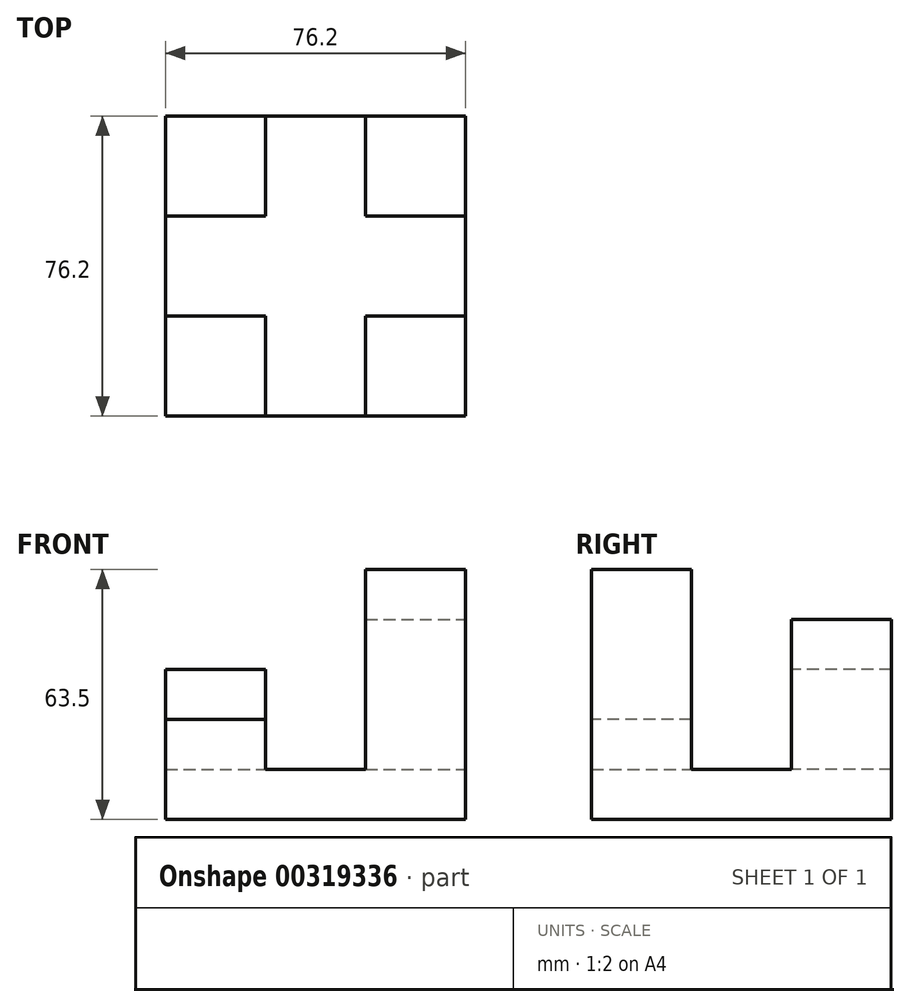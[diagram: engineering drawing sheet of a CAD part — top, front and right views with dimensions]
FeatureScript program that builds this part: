
annotation { "Feature Type Name" : "Feature", "Feature Type Description" : "" }
export const myFeature = defineFeature(function(context is Context, id is Id, definition is map)
    precondition{}
    {
        {
            var Q0;
            Q0=qCreatedBy(makeId("Top.planeOp"),FACE);
            var sketch = newSketch(context, id + "F0", { "sketchPlane" : qUnion([Q0])});
            skLineSegment(sketch, "E0.bottom", {"start": v(-38.59, 41.6) * mm, "end": v(37.61, 41.6) * mm});
            skLineSegment(sketch, "E0.top", {"start": v(-38.59, -34.6) * mm, "end": v(37.61, -34.6) * mm});
            skLineSegment(sketch, "E0.left", {"start": v(-38.59, 41.6) * mm, "end": v(-38.59, -34.6) * mm});
            skLineSegment(sketch, "E0.right", {"start": v(37.61, 41.6) * mm, "end": v(37.61, -34.6) * mm});
            skSolve(sketch);
        }
        {
            var Q0;
            Q0 = qSketchRegion(id + "F0", true);
            extrude(context, id + "F1", {"entities" : qUnion([Q0]), "depth" : 12.7 * mm});
        }
        {
            var Q0;
            Q0=makeQuery(id+"F1.opExtrude","CAP_FACE",FACE,{"disambiguationData":[OSD([sQuery(id+"F0.wireOp",EDGE,"E0.bottom"),sQuery(id+"F0.wireOp",EDGE,"E0.top"),sQuery(id+"F0.wireOp",EDGE,"E0.left"),sQuery(id+"F0.wireOp",EDGE,"E0.right")])],"isStart":false});
            var sketch = newSketch(context, id + "F2", { "sketchPlane" : qUnion([Q0])});
            skLineSegment(sketch, "E1", {"start": v(-38.59, -9.2) * mm, "end": v(-13.19, -9.2) * mm});
            skLineSegment(sketch, "E2", {"start": v(-13.19, -9.2) * mm, "end": v(-13.19, -34.6) * mm});
            skLineSegment(sketch, "E3", {"start": v(-13.19, -34.6) * mm, "end": v(-38.59, -34.6) * mm});
            skLineSegment(sketch, "E4", {"start": v(-38.59, -34.6) * mm, "end": v(-38.59, -9.2) * mm});
            skSolve(sketch);
        }
        {
            var Q0;
            Q0 = qSketchRegion(id + "F2", true);
            extrude(context, id + "F3", {"entities" : qUnion([Q0]), "operationType" : NewBodyOperationType.ADD, "depth" : 12.7 * mm});
        }
        {
            var Q0;
            Q0=makeQuery(id+"F1.opExtrude","CAP_FACE",FACE,{"disambiguationData":[OSD([sQuery(id+"F0.wireOp",EDGE,"E0.bottom"),sQuery(id+"F0.wireOp",EDGE,"E0.top"),sQuery(id+"F0.wireOp",EDGE,"E0.left"),sQuery(id+"F0.wireOp",EDGE,"E0.right")])],"isStart":false});
            var sketch = newSketch(context, id + "F4", { "sketchPlane" : qUnion([Q0])});
            skLineSegment(sketch, "E5", {"start": v(-38.59, 16.2) * mm, "end": v(-13.19, 16.2) * mm});
            skLineSegment(sketch, "E6", {"start": v(-13.19, 16.2) * mm, "end": v(-13.19, 41.6) * mm});
            skLineSegment(sketch, "E7", {"start": v(-13.19, 41.6) * mm, "end": v(-38.59, 41.6) * mm});
            skSolve(sketch);
        }
        {
            var Q0;
            Q0 = qSketchRegion(id + "F4", true);
            var Q1;
            {var subQ0=sQuery(id+"F4.wireOp",EDGE,"E5");Q1=makeQuery(id+"F4.imprint","IMPRINT",FACE,{"disambiguationData":[TD([[makeQuery(id+"F4.imprint","IMPRINT",EDGE,{"derivedFrom":subQ0}),1.0]])]});}
            extrude(context, id + "F5", {"entities" : qUnion([Q0, Q1]), "depth" : 25.4 * mm});
        }
        {
            var Q0;
            Q0=makeQuery(id+"F1.opExtrude","CAP_FACE",FACE,{"disambiguationData":[OSD([sQuery(id+"F0.wireOp",EDGE,"E0.bottom"),sQuery(id+"F0.wireOp",EDGE,"E0.top"),sQuery(id+"F0.wireOp",EDGE,"E0.left"),sQuery(id+"F0.wireOp",EDGE,"E0.right")])],"isStart":false});
            var sketch = newSketch(context, id + "F6", { "sketchPlane" : qUnion([Q0])});
            skLineSegment(sketch, "E8", {"start": v(12.21, 41.6) * mm, "end": v(12.21, 16.2) * mm});
            skLineSegment(sketch, "E9", {"start": v(12.21, 16.2) * mm, "end": v(37.61, 16.2) * mm});
            skLineSegment(sketch, "E10", {"start": v(37.61, 16.2) * mm, "end": v(37.61, 41.6) * mm});
            skLineSegment(sketch, "E11", {"start": v(37.61, 41.6) * mm, "end": v(12.21, 41.6) * mm});
            skSolve(sketch);
        }
        {
            var Q0;
            Q0 = qSketchRegion(id + "F6", true);
            extrude(context, id + "F7", {"entities" : qUnion([Q0]), "operationType" : NewBodyOperationType.ADD, "depth" : 38.1 * mm});
        }
        {
            var Q0;
            Q0=makeQuery(id+"F1.opExtrude","CAP_FACE",FACE,{"disambiguationData":[OSD([sQuery(id+"F0.wireOp",EDGE,"E0.bottom"),sQuery(id+"F0.wireOp",EDGE,"E0.top"),sQuery(id+"F0.wireOp",EDGE,"E0.left"),sQuery(id+"F0.wireOp",EDGE,"E0.right")])],"isStart":false});
            var sketch = newSketch(context, id + "F8", { "sketchPlane" : qUnion([Q0])});
            skLineSegment(sketch, "E12", {"start": v(12.21, -34.6) * mm, "end": v(12.21, -9.2) * mm});
            skLineSegment(sketch, "E13", {"start": v(12.21, -9.2) * mm, "end": v(37.61, -9.2) * mm});
            skLineSegment(sketch, "E14", {"start": v(37.61, -9.2) * mm, "end": v(37.61, -34.6) * mm});
            skLineSegment(sketch, "E15", {"start": v(37.61, -34.6) * mm, "end": v(12.21, -34.6) * mm});
            skSolve(sketch);
        }
        {
            var Q0;
            Q0 = qSketchRegion(id + "F8", true);
            extrude(context, id + "F9", {"entities" : qUnion([Q0]), "operationType" : NewBodyOperationType.ADD, "depth" : 50.8 * mm});
        }
    });
